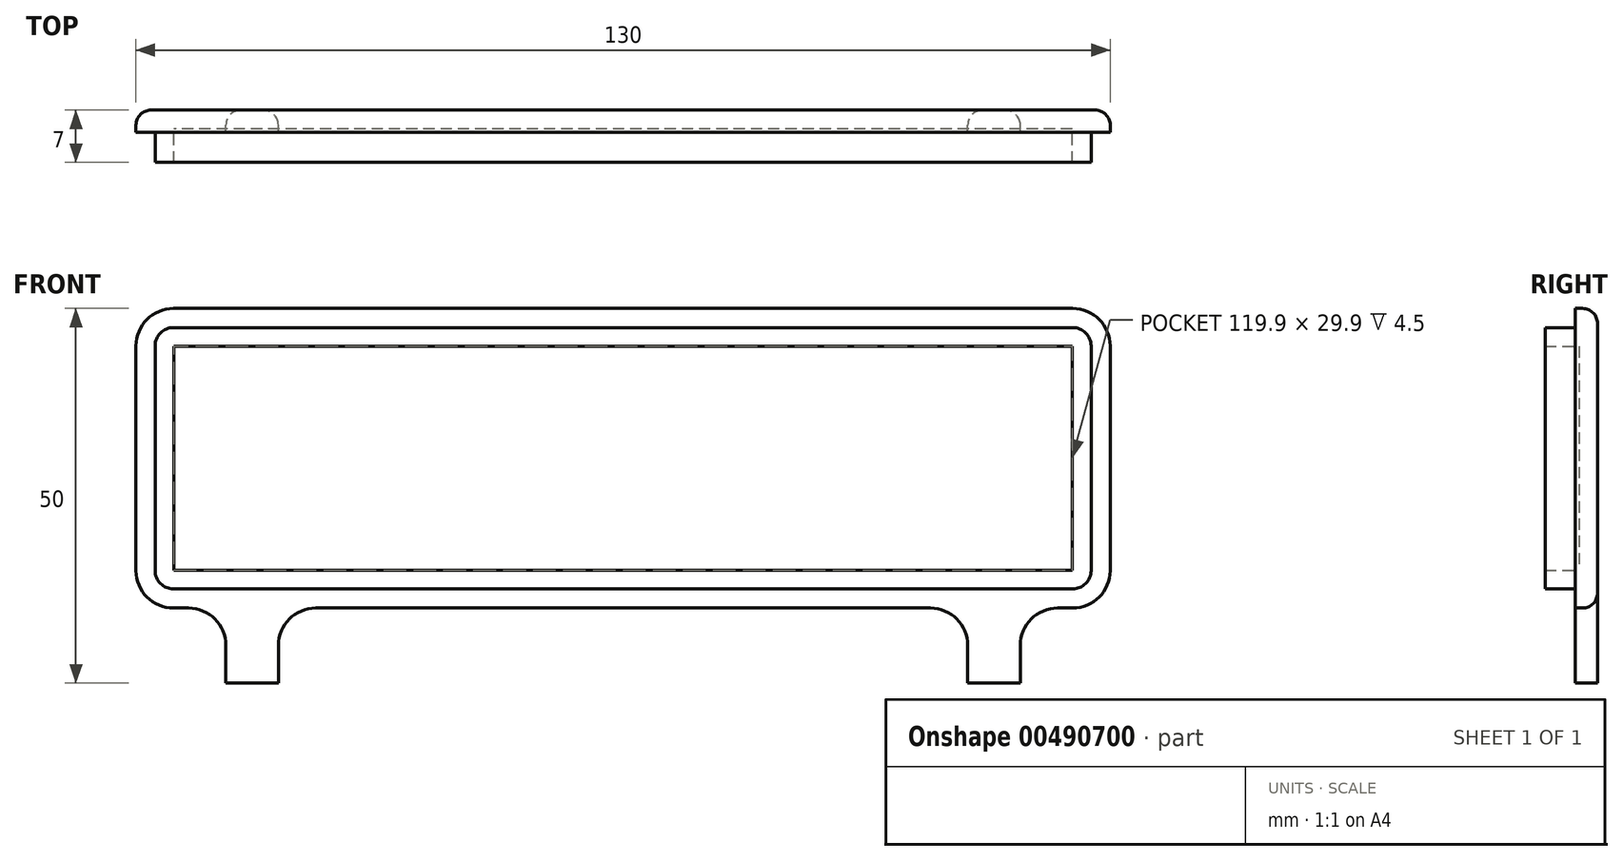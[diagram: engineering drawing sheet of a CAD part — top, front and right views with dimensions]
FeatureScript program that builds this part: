
annotation { "Feature Type Name" : "Feature", "Feature Type Description" : "" }
export const myFeature = defineFeature(function(context is Context, id is Id, definition is map)
    precondition{}
    {
        {
            var Q0;
            Q0=qCreatedBy(makeId("Front.planeOp"),FACE);
            var sketch = newSketch(context, id + "F0", { "sketchPlane" : qUnion([Q0])});
            skLineSegment(sketch, "E0.bottom", {"start": v(0, 0) * mm, "end": v(12, 0) * mm});
            skLineSegment(sketch, "E0.top", {"start": v(0, 40) * mm, "end": v(130, 40) * mm});
            skLineSegment(sketch, "E0.left", {"start": v(0, 0) * mm, "end": v(0, 40) * mm});
            skLineSegment(sketch, "E0.right", {"start": v(130, 0) * mm, "end": v(130, 40) * mm});
            skLineSegment(sketch, "E1.top", {"start": v(12, -10) * mm, "end": v(19, -10) * mm});
            skLineSegment(sketch, "E1.left", {"start": v(12, 0) * mm, "end": v(12, -10) * mm});
            skLineSegment(sketch, "E1.right", {"start": v(19, 0) * mm, "end": v(19, -10) * mm});
            skLineSegment(sketch, "E2", {"start": v(65, 40) * mm, "end": v(65, 0) * mm, "construction": true});
            skLineSegment(sketch, "E3.MirrorCS", {"start": v(118, 0) * mm, "end": v(118, -10) * mm});
            skLineSegment(sketch, "E4.MirrorCS", {"start": v(118, -10) * mm, "end": v(111, -10) * mm});
            skLineSegment(sketch, "E5.MirrorCS", {"start": v(111, 0) * mm, "end": v(111, -10) * mm});
            skLineSegment(sketch, "E6.trimOffspring", {"start": v(19, 0) * mm, "end": v(111, 0) * mm});
            skLineSegment(sketch, "E7.trimOffspring", {"start": v(118, 0) * mm, "end": v(130, 0) * mm});
            skSolve(sketch);
        }
        {
            var Q0;
            Q0 = qSketchRegion(id + "F0", true);
            extrude(context, id + "F1", {"entities" : qUnion([Q0]), "depth" : 3 * mm, "offsetDistance" : 25 * mm});
        }
        {
            var Q0;
            Q0=makeQuery(id+"F1.opExtrude","SWEPT_EDGE",EDGE,{"disambiguationData":[OSD([sQuery(id+"F0.wireOp",EDGE,"E0.top"),sQuery(id+"F0.wireOp",EDGE,"E0.right")])]});
            var Q1;
            Q1=makeQuery(id+"F1.opExtrude","SWEPT_EDGE",EDGE,{"disambiguationData":[OSD([sQuery(id+"F0.wireOp",EDGE,"E0.top"),sQuery(id+"F0.wireOp",EDGE,"E0.left")])]});
            var Q2;
            Q2=makeQuery(id+"F1.opExtrude","SWEPT_EDGE",EDGE,{"disambiguationData":[OSD([sQuery(id+"F0.wireOp",EDGE,"E0.bottom"),sQuery(id+"F0.wireOp",EDGE,"E0.left")])]});
            var Q3;
            Q3=makeQuery(id+"F1.opExtrude","SWEPT_EDGE",EDGE,{"disambiguationData":[OSD([sQuery(id+"F0.wireOp",EDGE,"E3.MirrorCS"),sQuery(id+"F0.wireOp",EDGE,"E7.trimOffspring")])]});
            var Q4;
            Q4=makeQuery(id+"F1.opExtrude","SWEPT_EDGE",EDGE,{"disambiguationData":[OSD([sQuery(id+"F0.wireOp",EDGE,"E0.right"),sQuery(id+"F0.wireOp",EDGE,"E7.trimOffspring")])]});
            var Q5;
            Q5=makeQuery(id+"F1.opExtrude","SWEPT_EDGE",EDGE,{"disambiguationData":[OSD([sQuery(id+"F0.wireOp",EDGE,"E5.MirrorCS"),sQuery(id+"F0.wireOp",EDGE,"E6.trimOffspring")])]});
            var Q6;
            Q6=makeQuery(id+"F1.opExtrude","SWEPT_EDGE",EDGE,{"disambiguationData":[OSD([sQuery(id+"F0.wireOp",EDGE,"E1.right"),sQuery(id+"F0.wireOp",EDGE,"E6.trimOffspring")])]});
            var Q7;
            Q7=makeQuery(id+"F1.opExtrude","SWEPT_EDGE",EDGE,{"disambiguationData":[OSD([sQuery(id+"F0.wireOp",EDGE,"E0.bottom"),sQuery(id+"F0.wireOp",EDGE,"E1.left")])]});
            fillet(context, id + "F2", {"entities" : qUnion([Q0, Q1, Q2, Q3, Q4, Q5, Q6, Q7]), "radius" : 5 * mm, "tangentPropagation" : true, "allowEdgeOverflow" : false});
        }
        {
            var Q0;
            Q0=makeQuery(id+"F1.opExtrude","CAP_FACE",FACE,{"disambiguationData":[OSD([sQuery(id+"F0.wireOp",EDGE,"E0.bottom"),sQuery(id+"F0.wireOp",EDGE,"E0.top"),sQuery(id+"F0.wireOp",EDGE,"E0.left"),sQuery(id+"F0.wireOp",EDGE,"E0.right"),sQuery(id+"F0.wireOp",EDGE,"E1.top"),sQuery(id+"F0.wireOp",EDGE,"E1.left"),sQuery(id+"F0.wireOp",EDGE,"E1.right"),sQuery(id+"F0.wireOp",EDGE,"E3.MirrorCS"),sQuery(id+"F0.wireOp",EDGE,"E4.MirrorCS"),sQuery(id+"F0.wireOp",EDGE,"E5.MirrorCS"),sQuery(id+"F0.wireOp",EDGE,"E6.trimOffspring"),sQuery(id+"F0.wireOp",EDGE,"E7.trimOffspring")])],"isStart":false});
            var sketch = newSketch(context, id + "F3", { "sketchPlane" : qUnion([Q0])});
            skLineSegment(sketch, "E8.0", {"start": v(5, 40) * mm, "end": v(125, 40) * mm, "construction": true});
            skArc(sketch, "E9.0", {"start": v(130, 35) * mm, "mid": v(128.54, 38.54) * mm, "end": v(125, 40) * mm, "construction": true});
            skLineSegment(sketch, "E10.0", {"start": v(130, 5) * mm, "end": v(130, 35) * mm, "construction": true});
            skArc(sketch, "E11.0", {"start": v(125, 0) * mm, "mid": v(128.54, 1.46) * mm, "end": v(130, 5) * mm, "construction": true});
            skLineSegment(sketch, "E12.0", {"start": v(5, 0) * mm, "end": v(125, 0) * mm, "construction": true});
            skLineSegment(sketch, "E13.0", {"start": v(0, 5) * mm, "end": v(0, 35) * mm, "construction": true});
            skArc(sketch, "E13.1", {"start": v(0, 5) * mm, "mid": v(1.46, 1.46) * mm, "end": v(5, 0) * mm, "construction": true});
            skArc(sketch, "E14.0", {"start": v(5, 40) * mm, "mid": v(1.46, 38.54) * mm, "end": v(0, 35) * mm, "construction": true});
            skPoint(sketch, "E15.orphan", {"position": v(24, 0) * mm});
            skPoint(sketch, "E16.orphan", {"position": v(106, 0) * mm});
            skArc(sketch, "E17.0", {"start": v(2.55, 5) * mm, "mid": v(3.27, 3.27) * mm, "end": v(5, 2.55) * mm});
            skLineSegment(sketch, "E17.1", {"start": v(2.55, 5) * mm, "end": v(2.55, 35) * mm});
            skLineSegment(sketch, "E17.2", {"start": v(5, 2.55) * mm, "end": v(125, 2.55) * mm});
            skArc(sketch, "E17.3", {"start": v(5, 37.45) * mm, "mid": v(3.27, 36.73) * mm, "end": v(2.55, 35) * mm});
            skArc(sketch, "E17.4", {"start": v(125, 2.55) * mm, "mid": v(126.73, 3.27) * mm, "end": v(127.45, 5) * mm});
            skLineSegment(sketch, "E17.5", {"start": v(127.45, 5) * mm, "end": v(127.45, 35) * mm});
            skArc(sketch, "E17.6", {"start": v(127.45, 35) * mm, "mid": v(126.73, 36.73) * mm, "end": v(125, 37.45) * mm});
            skLineSegment(sketch, "E17.7", {"start": v(5, 37.45) * mm, "end": v(125, 37.45) * mm});
            skSolve(sketch);
        }
        {
            var Q0;
            Q0 = qSketchRegion(id + "F3", true);
            extrude(context, id + "F4", {"entities" : qUnion([Q0]), "operationType" : NewBodyOperationType.ADD, "depth" : 4 * mm, "offsetDistance" : 25 * mm});
        }
        {
            var Q0;
            Q0=makeQuery(id+"F4.opExtrude","CAP_FACE",FACE,{"disambiguationData":[OSD([sQuery(id+"F3.wireOp",EDGE,"E17.0"),sQuery(id+"F3.wireOp",EDGE,"E17.1"),sQuery(id+"F3.wireOp",EDGE,"E17.2"),sQuery(id+"F3.wireOp",EDGE,"E17.3"),sQuery(id+"F3.wireOp",EDGE,"E17.4"),sQuery(id+"F3.wireOp",EDGE,"E17.5"),sQuery(id+"F3.wireOp",EDGE,"E17.6"),sQuery(id+"F3.wireOp",EDGE,"E17.7")])],"isStart":false});
            shell(context, id + "F5", {"entities" : qUnion([Q0]), "thickness" : 2.5 * mm});
        }
        {
            var Q0;
            Q0=makeQuery(id+"F1.opExtrude","CAP_EDGE",EDGE,{"disambiguationData":[OSD([sQuery(id+"F0.wireOp",EDGE,"E0.right")])],"isStart":true});
            var Q1;
            Q1=makeQuery(id+"F1.opExtrude","CAP_EDGE",EDGE,{"disambiguationData":[OSD([sQuery(id+"F0.wireOp",EDGE,"E6.trimOffspring")])],"isStart":true});
            fillet(context, id + "F6", {"entities" : qUnion([Q0, Q1]), "radius" : 2 * mm, "tangentPropagation" : true, "allowEdgeOverflow" : false});
        }
    });
